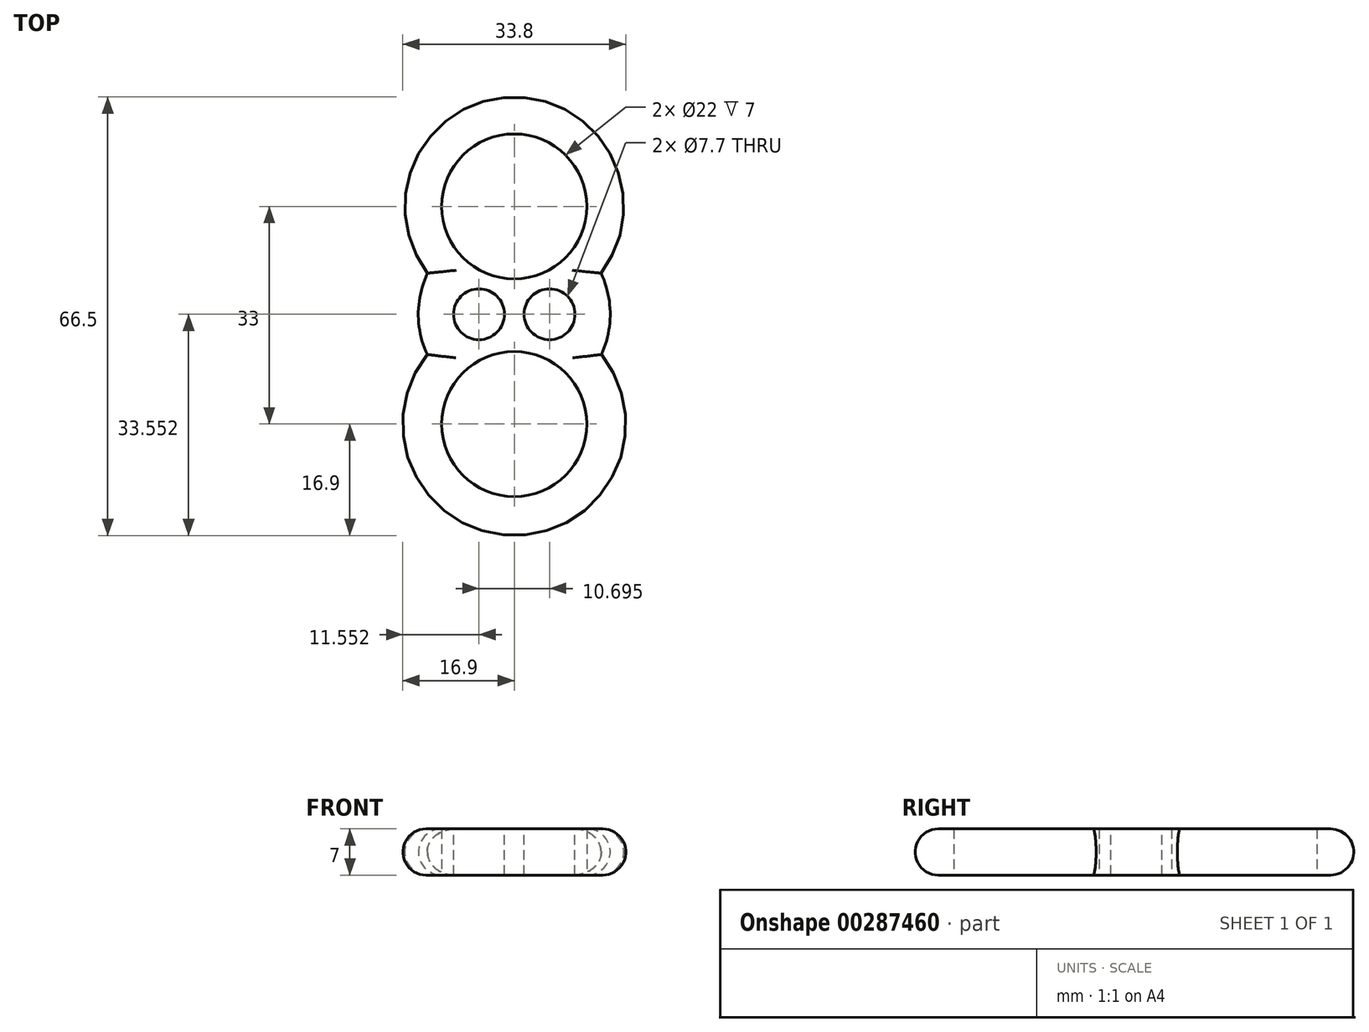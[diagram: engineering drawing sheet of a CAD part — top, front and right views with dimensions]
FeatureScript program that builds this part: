
annotation { "Feature Type Name" : "Feature", "Feature Type Description" : "" }
export const myFeature = defineFeature(function(context is Context, id is Id, definition is map)
    precondition{}
    {
        {
            var Q0;
            Q0=qCreatedBy(makeId("Top.planeOp"),FACE);
            var sketch = newSketch(context, id + "F0", { "sketchPlane" : qUnion([Q0])});
            skCircle(sketch, "E0", {"center": v(0, 0) * mm, "radius": 11 * mm});
            skCircle(sketch, "E1", {"center": v(0, 33) * mm, "radius": 11 * mm});
            skArc(sketch, "E2", {"start": v(13.15, 22.88) * mm, "mid": v(0, 49.6) * mm, "end": v(-13.15, 22.88) * mm});
            skLineSegment(sketch, "E3", {"start": v(0, 16.9) * mm, "end": v(0, 16.65) * mm});
            skArc(sketch, "E4", {"start": v(-13.15, 22.88) * mm, "mid": v(-14.55, 16.72) * mm, "end": v(-13.2, 10.55) * mm});
            skArc(sketch, "E5.trimOffspring", {"start": v(13.2, 10.55) * mm, "mid": v(14.55, 16.72) * mm, "end": v(13.15, 22.88) * mm});
            skArc(sketch, "E6.trimOffspring", {"start": v(-13.2, 10.55) * mm, "mid": v(0, -16.9) * mm, "end": v(13.2, 10.55) * mm});
            skPoint(sketch, "E7.orphan", {"position": v(0, 16.4) * mm});
            skSolve(sketch);
        }
        {
            var Q0;
            Q0=qSketchRegion(id+"F0",true);
            extrude(context, id + "F1", {"entities" : qUnion([Q0]), "depth" : 7 * mm});
        }
        {
            var Q0;
            Q0=makeQuery(id+"F1.opExtrude","CAP_EDGE",EDGE,{"disambiguationData":[OSD([sQuery(id+"F0.wireOp",EDGE,"E2")])],"isStart":false});
            var Q1;
            Q1=makeQuery(id+"F1.opExtrude","CAP_EDGE",EDGE,{"disambiguationData":[OSD([sQuery(id+"F0.wireOp",EDGE,"E4")])],"isStart":false});
            var Q2;
            Q2=makeQuery(id+"F1.opExtrude","CAP_EDGE",EDGE,{"disambiguationData":[OSD([sQuery(id+"F0.wireOp",EDGE,"E6.trimOffspring")])],"isStart":false});
            var Q3;
            Q3=makeQuery(id+"F1.opExtrude","CAP_EDGE",EDGE,{"disambiguationData":[OSD([sQuery(id+"F0.wireOp",EDGE,"E5.trimOffspring")])],"isStart":false});
            var Q4;
            Q4=makeQuery(id+"F1.opExtrude","CAP_EDGE",EDGE,{"disambiguationData":[OSD([sQuery(id+"F0.wireOp",EDGE,"E5.trimOffspring")])],"isStart":true});
            var Q5;
            Q5=makeQuery(id+"F1.opExtrude","CAP_EDGE",EDGE,{"disambiguationData":[OSD([sQuery(id+"F0.wireOp",EDGE,"E2")])],"isStart":true});
            var Q6;
            Q6=makeQuery(id+"F1.opExtrude","CAP_EDGE",EDGE,{"disambiguationData":[OSD([sQuery(id+"F0.wireOp",EDGE,"E6.trimOffspring")])],"isStart":true});
            var Q7;
            Q7=makeQuery(id+"F1.opExtrude","CAP_EDGE",EDGE,{"disambiguationData":[OSD([sQuery(id+"F0.wireOp",EDGE,"E4")])],"isStart":true});
            fillet(context, id + "F2", {"entities" : qUnion([Q0, Q1, Q2, Q3, Q4, Q5, Q6, Q7]), "radius" : 3.5 * mm, "tangentPropagation" : true, "allowEdgeOverflow" : false});
        }
        {
            var Q0;
            Q0=makeQuery(id+"F1.opExtrude","CAP_FACE",FACE,{"disambiguationData":[OSD([sQuery(id+"F0.wireOp",EDGE,"E0"),sQuery(id+"F0.wireOp",EDGE,"E1"),sQuery(id+"F0.wireOp",EDGE,"E2"),sQuery(id+"F0.wireOp",EDGE,"E4"),sQuery(id+"F0.wireOp",EDGE,"E5.trimOffspring"),sQuery(id+"F0.wireOp",EDGE,"E6.trimOffspring")])],"isStart":false});
            var sketch = newSketch(context, id + "F3", { "sketchPlane" : qUnion([Q0])});
            skCircle(sketch, "E8", {"center": v(5.35, 16.65) * mm, "radius": 3.85 * mm});
            skCircle(sketch, "E9", {"center": v(-5.35, 16.65) * mm, "radius": 3.85 * mm});
            skPoint(sketch, "E10.center.orphan", {"position": v(0, 16.65) * mm});
            skSolve(sketch);
        }
        {
            var Q0;
            Q0=makeQuery(id+"F3.imprint","IMPRINT",FACE,{"disambiguationData":[TD([[makeQuery(id+"F3.imprint","IMPRINT",EDGE,{"derivedFrom":sQuery(id+"F3.wireOp",EDGE,"E8")}),1.0]])]});
            var Q1;
            Q1=makeQuery(id+"F3.imprint","IMPRINT",FACE,{"disambiguationData":[TD([[makeQuery(id+"F3.imprint","IMPRINT",EDGE,{"derivedFrom":sQuery(id+"F3.wireOp",EDGE,"E9")}),1.0]])]});
            extrude(context, id + "F4", {"entities" : qUnion([Q0, Q1]), "operationType" : NewBodyOperationType.REMOVE, "endBound" : BoundingType.THROUGH_ALL, "oppositeDirection" : true, "depth" : 25 * mm});
        }
    });
